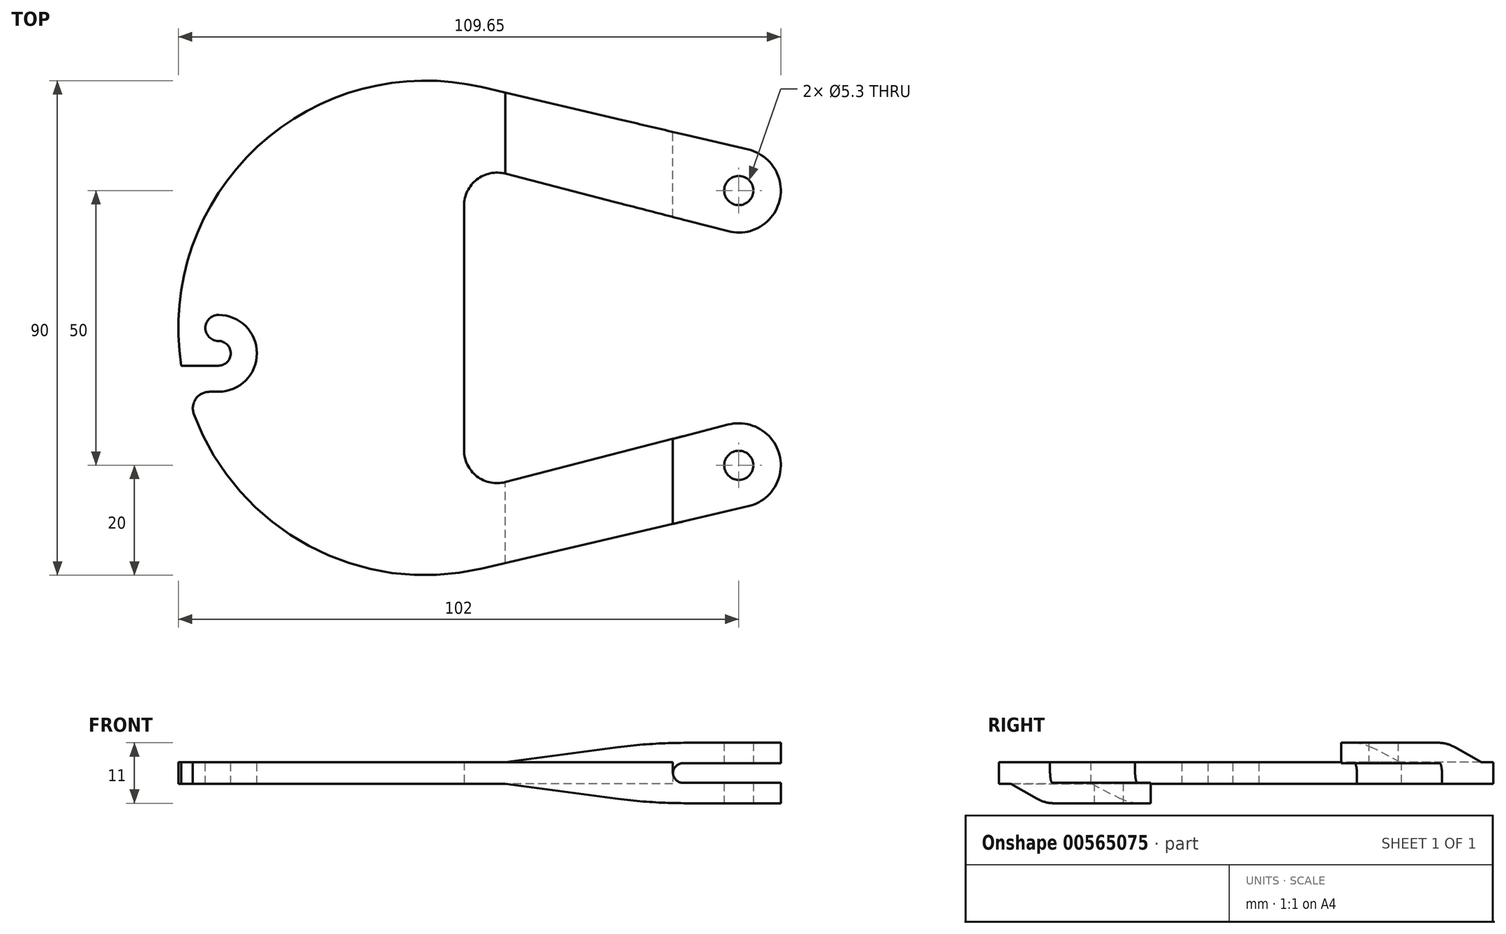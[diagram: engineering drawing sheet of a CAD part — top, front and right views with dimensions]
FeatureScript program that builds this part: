
annotation { "Feature Type Name" : "Feature", "Feature Type Description" : "" }
export const myFeature = defineFeature(function(context is Context, id is Id, definition is map)
    precondition{}
    {
        {
            var Q0;
            Q0=qCreatedBy(makeId("Top.planeOp"),FACE);
            var sketch = newSketch(context, id + "F0", { "sketchPlane" : qUnion([Q0])});
            skLineSegment(sketch, "E0", {"start": v(0, -25) * mm, "end": v(98, -25) * mm, "construction": true});
            skCircle(sketch, "E1", {"center": v(98, -25) * mm, "radius": 2.65 * mm});
            skLineSegment(sketch, "E2", {"start": v(0, 25) * mm, "end": v(98, 25) * mm, "construction": true});
            skLineSegment(sketch, "E3", {"start": v(0, 25) * mm, "end": v(0, 0) * mm, "construction": true});
            skLineSegment(sketch, "E4", {"start": v(0, 0) * mm, "end": v(0, -25) * mm, "construction": true});
            skCircle(sketch, "E5", {"center": v(98, 25) * mm, "radius": 2.65 * mm});
            skCircle(sketch, "E6.0", {"center": v(98, -25) * mm, "radius": 7.65 * mm});
            skLineSegment(sketch, "E7", {"start": v(51.27, -43.81) * mm, "end": v(99.75, -32.45) * mm});
            skCircle(sketch, "E8", {"center": v(98, 25) * mm, "radius": 7.65 * mm});
            skLineSegment(sketch, "E9", {"start": v(99.75, 32.45) * mm, "end": v(51.27, 43.81) * mm});
            skLineSegment(sketch, "E10", {"start": v(48, 22.26) * mm, "end": v(48, -22.26) * mm});
            skLineSegment(sketch, "E11", {"start": v(0, 0) * mm, "end": v(48, 0) * mm, "construction": true});
            skLineSegment(sketch, "E12", {"start": v(55.5, -28.07) * mm, "end": v(96.09, -17.6) * mm});
            skLineSegment(sketch, "E13", {"start": v(96.09, 17.6) * mm, "end": v(55.5, 28.07) * mm});
            skPoint(sketch, "E14.visualSharp", {"position": v(48, 30) * mm});
            skArc(sketch, "E14.filletArc", {"start": v(55.5, 28.07) * mm, "mid": v(50.33, 27) * mm, "end": v(48, 22.26) * mm});
            skPoint(sketch, "E15.visualSharp", {"position": v(48, -30) * mm});
            skArc(sketch, "E15.filletArc", {"start": v(48, -22.26) * mm, "mid": v(50.33, -27) * mm, "end": v(55.5, -28.07) * mm});
            skArc(sketch, "E16", {"start": v(51.27, 43.81) * mm, "mid": v(-4, 0) * mm, "end": v(51.27, -43.81) * mm});
            skSolve(sketch);
        }
        {
            var Q0;
            {var subQ3=sQuery(id+"F0.wireOp",EDGE,"E7");Q0=makeQuery(id+"F0.imprint","IMPRINT",FACE,{"disambiguationData":[TD([[makeQuery(id+"F0.imprint","IMPRINT",EDGE,{"derivedFrom":subQ3}),1.0]])]});}
            var Q1;
            Q1=makeQuery(id+"F0.imprint","IMPRINT",FACE,{"disambiguationData":[TD([[makeQuery(id+"F0.imprint","IMPRINT",EDGE,{"derivedFrom":sQuery(id+"F0.wireOp",EDGE,"E5")}),-1.0]])]});
            var Q2;
            Q2=makeQuery(id+"F0.imprint","IMPRINT",FACE,{"disambiguationData":[TD([[makeQuery(id+"F0.imprint","IMPRINT",EDGE,{"derivedFrom":sQuery(id+"F0.wireOp",EDGE,"E1")}),-1.0]])]});
            extrude(context, id + "F1", {"entities" : qUnion([Q0, Q1, Q2]), "depth" : 4 * mm, "offsetDistance" : 25 * mm});
        }
        {
            var Q0;
            Q0=makeQuery(id+"F1.opExtrude","CAP_FACE",FACE,{"disambiguationData":[OSD([sQuery(id+"F0.wireOp",EDGE,"xxKo6WRD-6QPB-TjOC-Ujmc-5RzxxUmcmt8J"),sQuery(id+"F0.wireOp",EDGE,"E1"),sQuery(id+"F0.wireOp",EDGE,"E5"),sQuery(id+"F0.wireOp",EDGE,"E6.0"),sQuery(id+"F0.wireOp",EDGE,"E7"),sQuery(id+"F0.wireOp",EDGE,"E8"),sQuery(id+"F0.wireOp",EDGE,"E9"),sQuery(id+"F0.wireOp",EDGE,"E10"),sQuery(id+"F0.wireOp",EDGE,"E12"),sQuery(id+"F0.wireOp",EDGE,"E13"),sQuery(id+"F0.wireOp",EDGE,"E14.filletArc"),sQuery(id+"F0.wireOp",EDGE,"E15.filletArc")])],"isStart":false});
            var sketch = newSketch(context, id + "F2", { "sketchPlane" : qUnion([Q0])});
            skArc(sketch, "E17", {"start": v(3.28, -11.63) * mm, "mid": v(10.28, -4.63) * mm, "end": v(3.28, 2.37) * mm});
            skPoint(sketch, "E17.centerSnap0", {"position": v(-4, 0) * mm});
            skArc(sketch, "E18", {"start": v(3.28, -6.88) * mm, "mid": v(5.53, -4.63) * mm, "end": v(3.28, -2.38) * mm});
            skArc(sketch, "E19", {"start": v(3.28, 2.37) * mm, "mid": v(0.9, 0) * mm, "end": v(3.28, -2.38) * mm});
            skLineSegment(sketch, "E20", {"start": v(3.28, -6.88) * mm, "end": v(-3.47, -6.88) * mm});
            skLineSegment(sketch, "E21", {"start": v(3.28, -11.63) * mm, "end": v(-2.47, -11.63) * mm});
            skLineSegment(sketch, "E22.0.0", {"start": v(99.75, -32.45) * mm, "end": v(51.27, -43.81) * mm});
            skArc(sketch, "E22.0.1", {"start": v(51.27, -43.81) * mm, "mid": v(-4, 0) * mm, "end": v(51.27, 43.81) * mm});
            skLineSegment(sketch, "E22.0.2", {"start": v(51.27, 43.81) * mm, "end": v(99.75, 32.45) * mm});
            skArc(sketch, "E22.0.3", {"start": v(99.75, 32.45) * mm, "mid": v(105.43, 23.17) * mm, "end": v(96.09, 17.6) * mm});
            skLineSegment(sketch, "E22.0.4", {"start": v(96.09, 17.6) * mm, "end": v(55.5, 28.07) * mm});
            skArc(sketch, "E22.0.5", {"start": v(55.5, 28.07) * mm, "mid": v(50.33, 27) * mm, "end": v(48, 22.26) * mm});
            skLineSegment(sketch, "E22.0.6", {"start": v(48, 22.26) * mm, "end": v(48, -22.26) * mm});
            skArc(sketch, "E22.0.7", {"start": v(48, -22.26) * mm, "mid": v(50.33, -27) * mm, "end": v(55.5, -28.07) * mm});
            skLineSegment(sketch, "E22.0.8", {"start": v(55.5, -28.07) * mm, "end": v(96.09, -17.6) * mm});
            skArc(sketch, "E22.0.9", {"start": v(96.09, -17.6) * mm, "mid": v(105.43, -23.17) * mm, "end": v(99.75, -32.45) * mm});
            skSolve(sketch);
        }
        {
            var Q0;
            Q0=makeQuery(id+"F2.imprint","IMPRINT",FACE,{"disambiguationData":[TD([[makeQuery(id+"F2.imprint","IMPRINT",EDGE,{"derivedFrom":sQuery(id+"F2.wireOp",EDGE,"E17")}),1.0]])]});
            extrude(context, id + "F3", {"entities" : qUnion([Q0]), "operationType" : NewBodyOperationType.REMOVE, "endBound" : BoundingType.THROUGH_ALL, "oppositeDirection" : true, "depth" : 25 * mm, "offsetDistance" : 25 * mm});
        }
        {
            var Q0;
            Q0=makeQuery(id+"F3.boolean.opBoolean","COPY",EDGE,{"derivedFrom":makeQuery(id+"F3.opExtrude","SWEPT_EDGE",EDGE,{"disambiguationData":[OSD([sQuery(id+"F0.wireOp",EDGE,"xxKo6WRD-6QPB-TjOC-Ujmc-5RzxxUmcmt8J"),sQuery(id+"F2.wireOp",EDGE,"E20")])]})});
            var Q1;
            Q1=makeQuery(id+"F3.boolean.opBoolean","COPY",EDGE,{"derivedFrom":makeQuery(id+"F3.opExtrude","SWEPT_EDGE",EDGE,{"disambiguationData":[OSD([sQuery(id+"F0.wireOp",EDGE,"xxKo6WRD-6QPB-TjOC-Ujmc-5RzxxUmcmt8J"),sQuery(id+"F2.wireOp",EDGE,"E21")])]})});
            fillet(context, id + "F4", {"entities" : qUnion([Q0, Q1]), "radius" : 3 * mm, "tangentPropagation" : true, "allowEdgeOverflow" : false});
        }
        {
            var Q0;
            Q0=makeQuery(id+"F1.opExtrude","CAP_FACE",FACE,{"disambiguationData":[OSD([sQuery(id+"F0.wireOp",EDGE,"xxKo6WRD-6QPB-TjOC-Ujmc-5RzxxUmcmt8J"),sQuery(id+"F0.wireOp",EDGE,"E1"),sQuery(id+"F0.wireOp",EDGE,"E5"),sQuery(id+"F0.wireOp",EDGE,"E6.0"),sQuery(id+"F0.wireOp",EDGE,"E7"),sQuery(id+"F0.wireOp",EDGE,"E8"),sQuery(id+"F0.wireOp",EDGE,"E9"),sQuery(id+"F0.wireOp",EDGE,"E10"),sQuery(id+"F0.wireOp",EDGE,"E12"),sQuery(id+"F0.wireOp",EDGE,"E13"),sQuery(id+"F0.wireOp",EDGE,"E14.filletArc"),sQuery(id+"F0.wireOp",EDGE,"E15.filletArc")])],"isStart":true});
            var sketch = newSketch(context, id + "F5", { "sketchPlane" : qUnion([Q0])});
            skArc(sketch, "E23.0.4", {"start": v(99.75, -32.45) * mm, "mid": v(105.43, -23.17) * mm, "end": v(96.09, -17.6) * mm});
            skLineSegment(sketch, "E23.0.5", {"start": v(96.09, -17.6) * mm, "end": v(55.5, -28.07) * mm});
            skArc(sketch, "E23.0.6", {"start": v(55.5, -28.07) * mm, "mid": v(50.33, -27) * mm, "end": v(48, -22.26) * mm});
            skLineSegment(sketch, "E23.0.7", {"start": v(48, -22.26) * mm, "end": v(48, 22.26) * mm});
            skLineSegment(sketch, "E23.0.9", {"start": v(55.5, 28.07) * mm, "end": v(96.09, 17.6) * mm});
            skArc(sketch, "E23.0.10", {"start": v(96.09, 17.6) * mm, "mid": v(105.43, 23.17) * mm, "end": v(99.75, 32.45) * mm});
            skLineSegment(sketch, "E23.0.11", {"start": v(99.75, 32.45) * mm, "end": v(51.27, 43.81) * mm});
            skCircle(sketch, "E24.0", {"center": v(98, 25) * mm, "radius": 2.65 * mm});
            skLineSegment(sketch, "E25", {"start": v(82, 36.6) * mm, "end": v(82, 21.23) * mm});
            skSolve(sketch);
        }
        {
            var Q0;
            {var subQ1=sQuery(id+"F5.wireOp",EDGE,"E23.0.10");Q0=makeQuery(id+"F5.imprint","IMPRINT",FACE,{"disambiguationData":[TD([[makeQuery(id+"F5.imprint","IMPRINT",EDGE,{"derivedFrom":subQ1}),-1.0]])]});}
            extrude(context, id + "F6", {"entities" : qUnion([Q0]), "operationType" : NewBodyOperationType.ADD, "depth" : 3.5 * mm, "offsetDistance" : 25 * mm});
        }
        {
            var Q0;
            Q0=makeQuery(id+"F1.opExtrude","CAP_FACE",FACE,{"disambiguationData":[OSD([sQuery(id+"F0.wireOp",EDGE,"xxKo6WRD-6QPB-TjOC-Ujmc-5RzxxUmcmt8J"),sQuery(id+"F0.wireOp",EDGE,"E1"),sQuery(id+"F0.wireOp",EDGE,"E5"),sQuery(id+"F0.wireOp",EDGE,"E6.0"),sQuery(id+"F0.wireOp",EDGE,"E7"),sQuery(id+"F0.wireOp",EDGE,"E8"),sQuery(id+"F0.wireOp",EDGE,"E9"),sQuery(id+"F0.wireOp",EDGE,"E10"),sQuery(id+"F0.wireOp",EDGE,"E12"),sQuery(id+"F0.wireOp",EDGE,"E13"),sQuery(id+"F0.wireOp",EDGE,"E14.filletArc"),sQuery(id+"F0.wireOp",EDGE,"E15.filletArc")])],"isStart":false});
            var sketch = newSketch(context, id + "F7", { "sketchPlane" : qUnion([Q0])});
            skLineSegment(sketch, "E26", {"start": v(86, -20.2) * mm, "end": v(86, -35.67) * mm});
            skArc(sketch, "E27.0.10", {"start": v(99.75, -32.45) * mm, "mid": v(105.43, -23.17) * mm, "end": v(96.09, -17.6) * mm});
            skLineSegment(sketch, "E27.0.11", {"start": v(96.09, -17.6) * mm, "end": v(55.5, -28.07) * mm});
            skArc(sketch, "E27.0.12", {"start": v(55.5, -28.07) * mm, "mid": v(50.33, -27) * mm, "end": v(48, -22.26) * mm});
            skLineSegment(sketch, "E27.0.13", {"start": v(48, -22.26) * mm, "end": v(48, 22.26) * mm});
            skArc(sketch, "E27.0.14", {"start": v(48, 22.26) * mm, "mid": v(50.33, 27) * mm, "end": v(55.5, 28.07) * mm});
            skLineSegment(sketch, "E27.0.15", {"start": v(55.5, 28.07) * mm, "end": v(96.09, 17.6) * mm});
            skArc(sketch, "E27.0.16", {"start": v(96.09, 17.6) * mm, "mid": v(105.43, 23.17) * mm, "end": v(99.75, 32.45) * mm});
            skCircle(sketch, "E28.0", {"center": v(98, -25) * mm, "radius": 2.65 * mm});
            skSolve(sketch);
        }
        {
            var Q0;
            {var subQ2=sQuery(id+"F7.wireOp",EDGE,"E26");Q0=makeQuery(id+"F7.imprint","IMPRINT",FACE,{"disambiguationData":[TD([[makeQuery(id+"F7.imprint","IMPRINT",EDGE,{"derivedFrom":subQ2}),1.0]])]});}
            extrude(context, id + "F8", {"entities" : qUnion([Q0]), "operationType" : NewBodyOperationType.REMOVE, "oppositeDirection" : true, "depth" : 3.8 * mm, "offsetDistance" : 25 * mm});
        }
        {
            var Q0;
            Q0=qCreatedBy(makeId("Front.planeOp"),FACE);
            var sketch = newSketch(context, id + "F9", { "sketchPlane" : qUnion([Q0])});
            skLineSegment(sketch, "E29.0", {"start": v(82, -3.5) * mm, "end": v(82, 0) * mm});
            skLineSegment(sketch, "E30.0", {"start": v(86, 0.2) * mm, "end": v(86, 4) * mm});
            skLineSegment(sketch, "E31.0", {"start": v(55.5, 0) * mm, "end": v(82, 0) * mm});
            skLineSegment(sketch, "E32.0", {"start": v(82, -3.5) * mm, "end": v(96.09, -3.5) * mm});
            skLineSegment(sketch, "E33", {"start": v(82, -3.5) * mm, "end": v(55.5, 0) * mm});
            skSolve(sketch);
        }
        {
            var Q0;
            Q0=makeQuery(id+"F9.imprint","IMPRINT",FACE,{"disambiguationData":[TD([[makeQuery(id+"F9.imprint","IMPRINT",EDGE,{"derivedFrom":sQuery(id+"F9.wireOp",EDGE,"E29.0")}),1.0]])]});
            var Q1;
            Q1=makeQuery(id+"F6.boolean.opBoolean","MERGE",FACE,{"derivedFrom":[makeQuery(id+"F1.opExtrude","SWEPT_FACE",FACE,{"disambiguationData":[OSD([sQuery(id+"F0.wireOp",EDGE,"E7")])]}),makeQuery(id+"F6.opExtrude","SWEPT_FACE",FACE,{"disambiguationData":[OSD([sQuery(id+"F5.wireOp",EDGE,"E23.0.11")])]})]});
            var Q2;
            Q2=makeQuery(id+"F6.boolean.opBoolean","MERGE",FACE,{"derivedFrom":[makeQuery(id+"F1.opExtrude","SWEPT_FACE",FACE,{"disambiguationData":[OSD([sQuery(id+"F0.wireOp",EDGE,"E12")])]}),makeQuery(id+"F6.opExtrude","SWEPT_FACE",FACE,{"disambiguationData":[OSD([sQuery(id+"F5.wireOp",EDGE,"E23.0.9")])]})]});
            extrude(context, id + "F10", {"entities" : qUnion([Q0]), "operationType" : NewBodyOperationType.ADD, "endBound" : BoundingType.UP_TO_SURFACE, "depth" : 25 * mm, "endBoundEntityFace" : qUnion([Q1]), "offsetDistance" : 25 * mm, "hasSecondDirection" : true, "secondDirectionBound" : SecondDirectionBoundingType.UP_TO_SURFACE, "secondDirectionOppositeDirection" : false, "secondDirectionDepth" : 25 * mm, "secondDirectionBoundEntityFace" : qUnion([Q2])});
        }
        {
            var Q0;
            Q0=makeQuery(id+"F1.opExtrude","CAP_FACE",FACE,{"disambiguationData":[OSD([sQuery(id+"F0.wireOp",EDGE,"xxKo6WRD-6QPB-TjOC-Ujmc-5RzxxUmcmt8J"),sQuery(id+"F0.wireOp",EDGE,"E1"),sQuery(id+"F0.wireOp",EDGE,"E5"),sQuery(id+"F0.wireOp",EDGE,"E6.0"),sQuery(id+"F0.wireOp",EDGE,"E7"),sQuery(id+"F0.wireOp",EDGE,"E8"),sQuery(id+"F0.wireOp",EDGE,"E9"),sQuery(id+"F0.wireOp",EDGE,"E10"),sQuery(id+"F0.wireOp",EDGE,"E12"),sQuery(id+"F0.wireOp",EDGE,"E13"),sQuery(id+"F0.wireOp",EDGE,"E14.filletArc"),sQuery(id+"F0.wireOp",EDGE,"E15.filletArc")])],"isStart":false});
            var sketch = newSketch(context, id + "F11", { "sketchPlane" : qUnion([Q0])});
            skArc(sketch, "E34.0.2", {"start": v(55.5, -28.07) * mm, "mid": v(50.33, -27) * mm, "end": v(48, -22.26) * mm});
            skLineSegment(sketch, "E34.0.3", {"start": v(48, -22.26) * mm, "end": v(48, 22.26) * mm});
            skArc(sketch, "E34.0.4", {"start": v(48, 22.26) * mm, "mid": v(50.33, 27) * mm, "end": v(55.5, 28.07) * mm});
            skLineSegment(sketch, "E34.0.5", {"start": v(55.5, 28.07) * mm, "end": v(96.09, 17.6) * mm});
            skArc(sketch, "E34.0.6", {"start": v(96.09, 17.6) * mm, "mid": v(105.43, 23.17) * mm, "end": v(99.75, 32.45) * mm});
            skLineSegment(sketch, "E34.0.7", {"start": v(99.75, 32.45) * mm, "end": v(99.75, 32.45) * mm});
            skLineSegment(sketch, "E34.0.14", {"start": v(3.28, -11.63) * mm, "end": v(1.63, -11.63) * mm});
            skCircle(sketch, "E35.0", {"center": v(98, 25) * mm, "radius": 2.65 * mm});
            skLineSegment(sketch, "E36", {"start": v(82, 21.23) * mm, "end": v(82, 36.6) * mm});
            skLineSegment(sketch, "E37.0.7", {"start": v(99.75, 32.45) * mm, "end": v(51.27, 43.81) * mm});
            skArc(sketch, "E37.0.16", {"start": v(-1.18, -15.67) * mm, "mid": v(19.73, -39.65) * mm, "end": v(51.27, -43.81) * mm});
            skArc(sketch, "E38.0.8", {"start": v(51.27, 43.81) * mm, "mid": v(11.45, 33.94) * mm, "end": v(-3.8, -4.15) * mm});
            skArc(sketch, "E38.0.9", {"start": v(-3.8, -4.15) * mm, "mid": v(-2.84, -6.1) * mm, "end": v(-0.82, -6.88) * mm});
            skLineSegment(sketch, "E38.0.10", {"start": v(-0.82, -6.88) * mm, "end": v(3.28, -6.88) * mm});
            skArc(sketch, "E38.0.11", {"start": v(3.28, -6.88) * mm, "mid": v(5.53, -4.63) * mm, "end": v(3.28, -2.38) * mm});
            skArc(sketch, "E38.0.12", {"start": v(3.28, -2.38) * mm, "mid": v(0.9, 0) * mm, "end": v(3.28, 2.37) * mm});
            skArc(sketch, "E38.0.13", {"start": v(3.28, 2.37) * mm, "mid": v(10.28, -4.63) * mm, "end": v(3.28, -11.63) * mm});
            skArc(sketch, "E38.0.15", {"start": v(1.63, -11.63) * mm, "mid": v(-0.83, -12.91) * mm, "end": v(-1.18, -15.67) * mm});
            skSolve(sketch);
        }
        {
            var Q0;
            Q0=makeQuery(id+"F11.imprint","IMPRINT",FACE,{"disambiguationData":[TD([[makeQuery(id+"F11.imprint","IMPRINT",EDGE,{"derivedFrom":sQuery(id+"F11.wireOp",EDGE,"E35.0")}),-1.0]])]});
            extrude(context, id + "F12", {"entities" : qUnion([Q0]), "operationType" : NewBodyOperationType.ADD, "depth" : 3.5 * mm, "offsetDistance" : 25 * mm});
        }
        {
            var Q0;
            Q0=makeQuery(id+"F1.opExtrude","CAP_FACE",FACE,{"disambiguationData":[OSD([sQuery(id+"F0.wireOp",EDGE,"xxKo6WRD-6QPB-TjOC-Ujmc-5RzxxUmcmt8J"),sQuery(id+"F0.wireOp",EDGE,"E1"),sQuery(id+"F0.wireOp",EDGE,"E5"),sQuery(id+"F0.wireOp",EDGE,"E6.0"),sQuery(id+"F0.wireOp",EDGE,"E7"),sQuery(id+"F0.wireOp",EDGE,"E8"),sQuery(id+"F0.wireOp",EDGE,"E9"),sQuery(id+"F0.wireOp",EDGE,"E10"),sQuery(id+"F0.wireOp",EDGE,"E12"),sQuery(id+"F0.wireOp",EDGE,"E13"),sQuery(id+"F0.wireOp",EDGE,"E14.filletArc"),sQuery(id+"F0.wireOp",EDGE,"E15.filletArc")])],"isStart":true});
            var sketch = newSketch(context, id + "F13", { "sketchPlane" : qUnion([Q0])});
            skLineSegment(sketch, "E39", {"start": v(86, -20.2) * mm, "end": v(86, -35.67) * mm});
            skLineSegment(sketch, "E40.0.0", {"start": v(55.5, 28.07) * mm, "end": v(55.5, 42.82) * mm});
            skLineSegment(sketch, "E40.0.1", {"start": v(55.5, 42.82) * mm, "end": v(51.27, 43.81) * mm});
            skArc(sketch, "E40.0.12", {"start": v(99.75, -32.45) * mm, "mid": v(105.43, -23.17) * mm, "end": v(96.09, -17.6) * mm});
            skLineSegment(sketch, "E40.0.13", {"start": v(96.09, -17.6) * mm, "end": v(55.5, -28.07) * mm});
            skArc(sketch, "E40.0.14", {"start": v(55.5, -28.07) * mm, "mid": v(50.33, -27) * mm, "end": v(48, -22.26) * mm});
            skLineSegment(sketch, "E40.0.15", {"start": v(48, -22.26) * mm, "end": v(48, 22.26) * mm});
            skArc(sketch, "E40.0.16", {"start": v(48, 22.26) * mm, "mid": v(50.33, 27) * mm, "end": v(55.5, 28.07) * mm});
            skCircle(sketch, "E41.0", {"center": v(98, -25) * mm, "radius": 2.65 * mm});
            skArc(sketch, "E42.0.2", {"start": v(51.27, 43.81) * mm, "mid": v(19.73, 39.65) * mm, "end": v(-1.18, 15.67) * mm});
            skArc(sketch, "E42.0.3", {"start": v(-1.18, 15.67) * mm, "mid": v(-0.83, 12.91) * mm, "end": v(1.63, 11.63) * mm});
            skLineSegment(sketch, "E42.0.4", {"start": v(1.63, 11.63) * mm, "end": v(3.28, 11.63) * mm});
            skArc(sketch, "E42.0.5", {"start": v(3.28, 11.63) * mm, "mid": v(10.28, 4.63) * mm, "end": v(3.28, -2.37) * mm});
            skArc(sketch, "E42.0.6", {"start": v(3.28, -2.37) * mm, "mid": v(0.9, 0) * mm, "end": v(3.28, 2.38) * mm});
            skArc(sketch, "E42.0.7", {"start": v(3.28, 2.38) * mm, "mid": v(5.53, 4.63) * mm, "end": v(3.28, 6.88) * mm});
            skLineSegment(sketch, "E42.0.8", {"start": v(3.28, 6.88) * mm, "end": v(-0.82, 6.88) * mm});
            skArc(sketch, "E42.0.9", {"start": v(-0.82, 6.88) * mm, "mid": v(-2.84, 6.1) * mm, "end": v(-3.8, 4.15) * mm});
            skArc(sketch, "E42.0.10", {"start": v(-3.8, 4.15) * mm, "mid": v(11.45, -33.94) * mm, "end": v(51.27, -43.81) * mm});
            skLineSegment(sketch, "E42.0.11", {"start": v(51.27, -43.81) * mm, "end": v(99.75, -32.45) * mm});
            skSolve(sketch);
        }
        {
            var Q0;
            {var subQ2=sQuery(id+"F13.wireOp",EDGE,"E39");Q0=makeQuery(id+"F13.imprint","IMPRINT",FACE,{"disambiguationData":[TD([[makeQuery(id+"F13.imprint","IMPRINT",EDGE,{"derivedFrom":subQ2}),1.0]])]});}
            extrude(context, id + "F14", {"entities" : qUnion([Q0]), "operationType" : NewBodyOperationType.REMOVE, "oppositeDirection" : true, "depth" : 3.8 * mm, "offsetDistance" : 25 * mm});
        }
        {
            var Q0;
            Q0=qCreatedBy(makeId("Front.planeOp"),FACE);
            var sketch = newSketch(context, id + "F15", { "sketchPlane" : qUnion([Q0])});
            skLineSegment(sketch, "E43.0", {"start": v(82, 4) * mm, "end": v(82, 7.5) * mm});
            skLineSegment(sketch, "E44.0", {"start": v(82, 4) * mm, "end": v(51.27, 4) * mm});
            skLineSegment(sketch, "E45.0", {"start": v(82, 4) * mm, "end": v(55.5, 4) * mm});
            skLineSegment(sketch, "E46", {"start": v(82, 7.5) * mm, "end": v(55.5, 4) * mm});
            skSolve(sketch);
        }
        {
            var Q0;
            Q0=makeQuery(id+"F15.imprint","IMPRINT",FACE,{"disambiguationData":[TD([[makeQuery(id+"F15.imprint","IMPRINT",EDGE,{"derivedFrom":sQuery(id+"F15.wireOp",EDGE,"E43.0")}),1.0]])]});
            var Q1;
            Q1=makeQuery(id+"F12.boolean.opBoolean","MERGE",FACE,{"derivedFrom":[makeQuery(id+"F1.opExtrude","SWEPT_FACE",FACE,{"disambiguationData":[OSD([sQuery(id+"F0.wireOp",EDGE,"E9")])]}),makeQuery(id+"F12.opExtrude","SWEPT_FACE",FACE,{"disambiguationData":[OSD([sQuery(id+"F11.wireOp",EDGE,"E37.0.7")])]})]});
            var Q2;
            Q2=makeQuery(id+"F12.boolean.opBoolean","MERGE",FACE,{"derivedFrom":[makeQuery(id+"F1.opExtrude","SWEPT_FACE",FACE,{"disambiguationData":[OSD([sQuery(id+"F0.wireOp",EDGE,"E13")])]}),makeQuery(id+"F12.opExtrude","SWEPT_FACE",FACE,{"disambiguationData":[OSD([sQuery(id+"F11.wireOp",EDGE,"E34.0.5")])]})]});
            extrude(context, id + "F16", {"entities" : qUnion([Q0]), "operationType" : NewBodyOperationType.ADD, "endBound" : BoundingType.UP_TO_SURFACE, "oppositeDirection" : true, "depth" : 25 * mm, "endBoundEntityFace" : qUnion([Q1]), "offsetDistance" : 25 * mm, "hasSecondDirection" : true, "secondDirectionBound" : SecondDirectionBoundingType.UP_TO_SURFACE, "secondDirectionOppositeDirection" : true, "secondDirectionDepth" : 25 * mm, "secondDirectionBoundEntityFace" : qUnion([Q2])});
        }
        {
            var Q0;
            Q0=makeQuery(id+"F14.boolean.opBoolean","COPY",EDGE,{"derivedFrom":makeQuery(id+"F14.opExtrude","CAP_EDGE",EDGE,{"disambiguationData":[OSD([sQuery(id+"F13.wireOp",EDGE,"E39")])],"isStart":true})});
            var Q1;
            Q1=makeQuery(id+"F14.boolean.opBoolean","COPY",EDGE,{"derivedFrom":makeQuery(id+"F14.opExtrude","CAP_EDGE",EDGE,{"disambiguationData":[OSD([sQuery(id+"F13.wireOp",EDGE,"E39")])],"isStart":false})});
            var Q2;
            Q2=makeQuery(id+"F8.boolean.opBoolean","COPY",EDGE,{"derivedFrom":makeQuery(id+"F8.opExtrude","CAP_EDGE",EDGE,{"disambiguationData":[OSD([sQuery(id+"F7.wireOp",EDGE,"E26")])],"isStart":false})});
            var Q3;
            Q3=makeQuery(id+"F8.boolean.opBoolean","COPY",EDGE,{"derivedFrom":makeQuery(id+"F8.opExtrude","CAP_EDGE",EDGE,{"disambiguationData":[OSD([sQuery(id+"F7.wireOp",EDGE,"E26")])],"isStart":true})});
            fillet(context, id + "F17", {"entities" : qUnion([Q0, Q1, Q2, Q3]), "radius" : 1.9 * mm, "tangentPropagation" : true, "allowEdgeOverflow" : false});
        }
        {
            var Q0;
            Q0=makeQuery(id+"F10.opExtrude","TWEAK_EDGE",EDGE,{"derivedFrom":[makeQuery(id+"F9.imprint","IMPRINT",EDGE,{"derivedFrom":sQuery(id+"F9.wireOp",EDGE,"E31.0")}),makeQuery(id+"F9.imprint","IMPRINT",EDGE,{"derivedFrom":sQuery(id+"F9.wireOp",EDGE,"E33")})]});
            var Q1;
            Q1=makeQuery(id+"F10.boolean.opBoolean","MERGE",EDGE,{"derivedFrom":[makeQuery(id+"F6.opExtrude","CAP_EDGE",EDGE,{"disambiguationData":[OSD([sQuery(id+"F5.wireOp",EDGE,"E25")])],"isStart":false}),makeQuery(id+"F10.opExtrude","TWEAK_EDGE",EDGE,{"derivedFrom":[makeQuery(id+"F9.imprint","IMPRINT",EDGE,{"derivedFrom":sQuery(id+"F9.wireOp",EDGE,"E29.0")}),makeQuery(id+"F9.imprint","IMPRINT",EDGE,{"derivedFrom":sQuery(id+"F9.wireOp",EDGE,"E33")})]})]});
            var Q2;
            Q2=makeQuery(id+"F16.opExtrude","TWEAK_EDGE",EDGE,{"derivedFrom":[makeQuery(id+"F15.imprint","IMPRINT",EDGE,{"derivedFrom":sQuery(id+"F15.wireOp",EDGE,"E45.0")}),makeQuery(id+"F15.imprint","IMPRINT",EDGE,{"derivedFrom":sQuery(id+"F15.wireOp",EDGE,"E46")})]});
            var Q3;
            Q3=makeQuery(id+"F16.boolean.opBoolean","MERGE",EDGE,{"derivedFrom":[makeQuery(id+"F12.opExtrude","CAP_EDGE",EDGE,{"disambiguationData":[OSD([sQuery(id+"F11.wireOp",EDGE,"E36")])],"isStart":false}),makeQuery(id+"F16.opExtrude","TWEAK_EDGE",EDGE,{"derivedFrom":[makeQuery(id+"F15.imprint","IMPRINT",EDGE,{"derivedFrom":sQuery(id+"F15.wireOp",EDGE,"E43.0")}),makeQuery(id+"F15.imprint","IMPRINT",EDGE,{"derivedFrom":sQuery(id+"F15.wireOp",EDGE,"E46")})]})]});
            fillet(context, id + "F18", {"entities" : qUnion([Q0, Q1, Q2, Q3]), "radius" : 100 * mm, "tangentPropagation" : true, "allowEdgeOverflow" : false});
        }
    });
